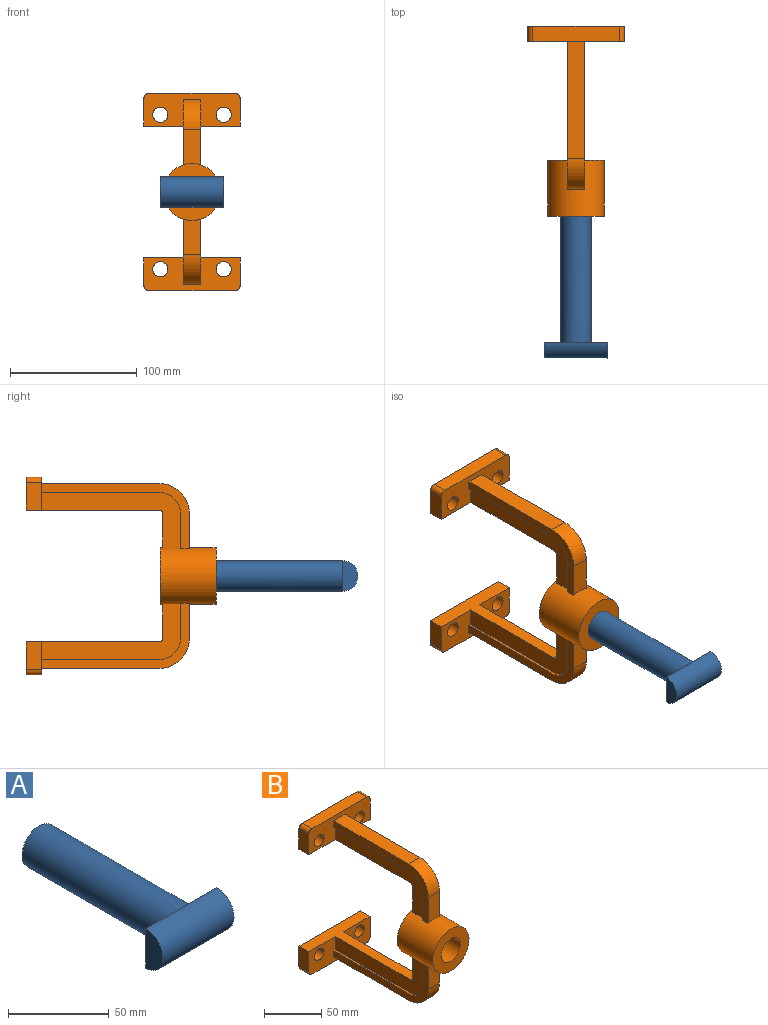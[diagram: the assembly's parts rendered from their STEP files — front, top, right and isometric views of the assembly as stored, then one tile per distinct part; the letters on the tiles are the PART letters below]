
ASSEMBLY  parts=2 mates=1
PART A: 7 faces, bbox 50x112x24 mm
  f0: cylinder r=12mm len=100mm, axis (0,-1,0), area 7539.8mm2, adj f1,f2,f3
  f1: plane 24x24mm, normal (0,1,0), area 452.4mm2, adj f0
  f2: plane 25x24mm, normal (0,1,0), area 373.8mm2, adj f0,f4,f5
  f3: plane 25x24mm, normal (0,1,0), area 373.8mm2, adj f0,f4,f6
  f4: cylinder r=12mm len=50mm, axis (-1,0,0), area 1885mm2, adj f2,f3,f5,f6
  f5: plane 24x12mm, normal (1,0,0), area 226.2mm2, adj f2,f4
  f6: plane 24x12mm, normal (-1,0,0), area 226.2mm2, adj f3,f4
PART B: 54 faces, bbox 76x150x156 mm
  f0: cylinder r=12mm len=44mm, axis (0,1,0), area 3317.5mm2, adj f2,f3
  f1: cylinder r=22.5mm len=45mm, axis (0,1,0), area 5738.7mm2, adj f2,f3,f4,f5,f6,f7,f21,f22
  f2: plane 45x45mm, normal (0,-1,0), area 1138mm2, adj f0,f1
  f3: plane 45x45mm, normal (0,1,0), area 1138mm2, adj f0,f1
  f4: plane 110x44.07mm, normal (-1,0,0), area 1900.8mm2, adj f1,f9,f10,f16,f17,f20,f21,f24
  f5: plane 110x44.07mm, normal (1,0,0), area 1900.8mm2, adj f1,f9,f10,f14,f17,f18,f21,f22
  f6: plane 117x51.62mm, normal (1,0,0), area 1069.7mm2, adj f1,f9,f14,f15,f18,f19,f22,f23
  f7: plane 117x51.62mm, normal (-1,0,0), area 1069.7mm2, adj f1,f9,f15,f16,f19,f20,f23,f24
  f8: plane 76x26mm, normal (0,1,0), area 1742.9mm2, adj f10,f11,f12,f13,f25,f26,f27,f28
  f9: plane 76x26mm, normal (0,-1,0), area 1504.9mm2, adj f4,f5,f6,f7,f10,f11,f12,f13
  f10: plane 104.61x76mm, normal (0,0,-1), area 1838.1mm2, adj f4,f5,f8,f9,f12,f13,f17
  f11: plane 68x12mm, normal (0,0,1), area 816mm2, adj f8,f9,f25,f26
  f12: plane 22x12mm, normal (1,0,0), area 264mm2, adj f8,f9,f10,f26
  f13: plane 22x12mm, normal (-1,0,0), area 264mm2, adj f8,f9,f10,f25
  f14: plane 92.61x2mm, normal (0,0,-1), area 185.2mm2, adj f5,f6,f9,f18
  f15: plane 92.61x14mm, normal (0,0,1), area 1296.5mm2, adj f6,f7,f9,f19
  f16: plane 92.61x2mm, normal (0,0,-1), area 185.2mm2, adj f4,f7,f9,f20
  f17: cylinder r=3.03mm len=10mm, axis (1,0,0), area 47.5mm2, adj f4,f5,f10,f21
  f18: cylinder r=17mm len=17.39mm, axis (1,0,0), area 53.4mm2, adj f5,f6,f14,f22
  f19: cylinder r=24mm len=24.39mm, axis (1,0,0), area 527.9mm2, adj f6,f7,f15,f23
  f20: cylinder r=17mm len=17.39mm, axis (1,0,0), area 53.4mm2, adj f4,f7,f16,f24
  f21: plane 27.45x10mm, normal (0,1,0), area 270.8mm2, adj f1,f4,f5,f17
  f22: plane 28.01x2mm, normal (0,1,0), area 55.4mm2, adj f1,f5,f6,f18
  f23: plane 28.01x14mm, normal (0,-1,0), area 381.6mm2, adj f1,f6,f7,f19
  f24: plane 28.01x2mm, normal (0,1,0), area 55.4mm2, adj f1,f4,f7,f20
  f25: cylinder r=4mm len=12mm, axis (0,-1,0), area 75.4mm2, adj f8,f9,f11,f13
  f26: cylinder r=4mm len=12mm, axis (0,1,0), area 75.4mm2, adj f8,f9,f11,f12
  f27: cylinder r=6mm len=12mm, axis (0,-1,0), area 452.4mm2, adj f8,f9
  f28: cylinder r=6mm len=12mm, axis (0,-1,0), area 452.4mm2, adj f8,f9
  f29: plane 110x44.07mm, normal (-1,0,0), area 1900.8mm2, adj f1,f34,f35,f41,f42,f45,f46,f49
  f30: plane 110x44.07mm, normal (1,0,0), area 1900.8mm2, adj f1,f34,f35,f39,f42,f43,f46,f47
  f31: plane 117x51.62mm, normal (1,0,0), area 1069.7mm2, adj f1,f34,f39,f40,f43,f44,f47,f48
  f32: plane 117x51.62mm, normal (-1,0,0), area 1069.7mm2, adj f1,f34,f40,f41,f44,f45,f48,f49
  f33: plane 76x26mm, normal (0,1,0), area 1742.9mm2, adj f35,f36,f37,f38,f50,f51,f52,f53
  f34: plane 76x26mm, normal (0,-1,0), area 1504.9mm2, adj f29,f30,f31,f32,f35,f36,f37,f38
  f35: plane 104.61x76mm, normal (0,0,1), area 1838.1mm2, adj f29,f30,f33,f34,f37,f38,f42
  f36: plane 68x12mm, normal (0,0,-1), area 816mm2, adj f33,f34,f50,f51
  f37: plane 22x12mm, normal (1,0,0), area 264mm2, adj f33,f34,f35,f51
  f38: plane 22x12mm, normal (-1,0,0), area 264mm2, adj f33,f34,f35,f50
  f39: plane 92.61x2mm, normal (0,0,1), area 185.2mm2, adj f30,f31,f34,f43
  f40: plane 92.61x14mm, normal (0,0,-1), area 1296.5mm2, adj f31,f32,f34,f44
  f41: plane 92.61x2mm, normal (0,0,1), area 185.2mm2, adj f29,f32,f34,f45
  f42: cylinder r=3.03mm len=10mm, axis (1,0,0), area 47.5mm2, adj f29,f30,f35,f46
  f43: cylinder r=17mm len=17.39mm, axis (1,0,0), area 53.4mm2, adj f30,f31,f39,f47
  f44: cylinder r=24mm len=24.39mm, axis (1,0,0), area 527.9mm2, adj f31,f32,f40,f48
  f45: cylinder r=17mm len=17.39mm, axis (1,0,0), area 53.4mm2, adj f29,f32,f41,f49
  f46: plane 27.45x10mm, normal (0,1,0), area 270.8mm2, adj f1,f29,f30,f42
  f47: plane 28.01x2mm, normal (0,1,0), area 55.4mm2, adj f1,f30,f31,f43
  f48: plane 28.01x14mm, normal (0,-1,0), area 381.6mm2, adj f1,f31,f32,f44
  f49: plane 28.01x2mm, normal (0,1,0), area 55.4mm2, adj f1,f29,f32,f45
  f50: cylinder r=4mm len=12mm, axis (0,-1,0), area 75.4mm2, adj f33,f34,f36,f38
  f51: cylinder r=4mm len=12mm, axis (0,1,0), area 75.4mm2, adj f33,f34,f36,f37
  f52: cylinder r=6mm len=12mm, axis (0,-1,0), area 452.4mm2, adj f33,f34
  f53: cylinder r=6mm len=12mm, axis (0,-1,0), area 452.4mm2, adj f33,f34
PLACE A t=(-70.73,-234.12,110.35)mm
PLACE B rot(axis=(0,1,0),0deg) t=(-70.73,-90.12,110.35)mm
MATE revolute A.f0 <-> B.f0  axis (0,-1,0) through (-70.73,-134.12,110.35)mm
